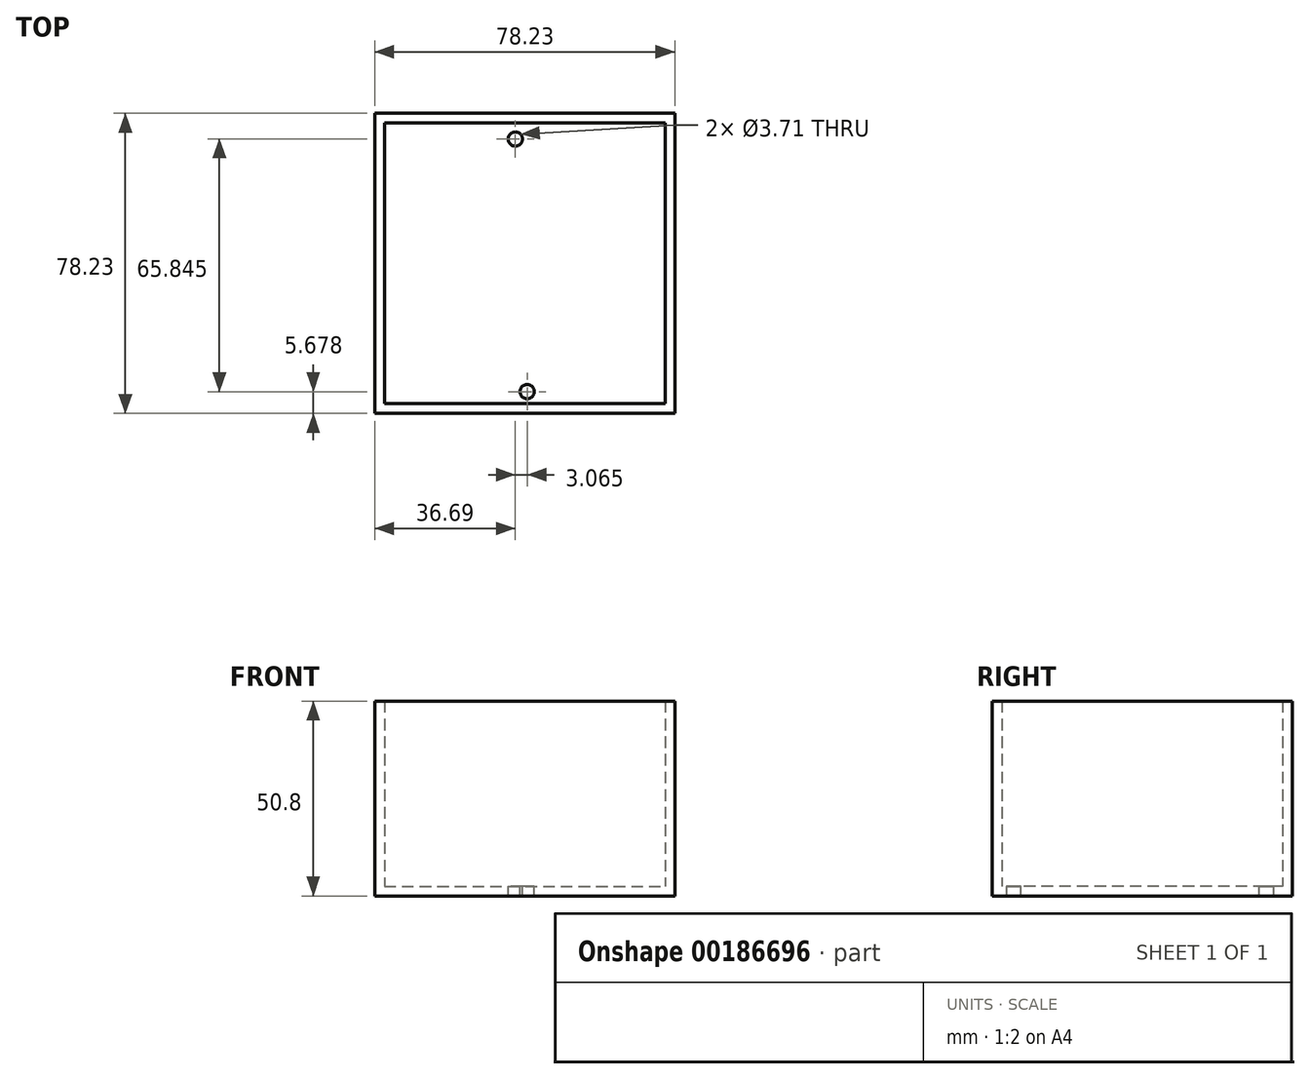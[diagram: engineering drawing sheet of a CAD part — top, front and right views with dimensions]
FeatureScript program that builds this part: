
annotation { "Feature Type Name" : "Feature", "Feature Type Description" : "" }
export const myFeature = defineFeature(function(context is Context, id is Id, definition is map)
    precondition{}
    {
        {
            var Q0;
            Q0=qCreatedBy(makeId("Top.planeOp"),FACE);
            var sketch = newSketch(context, id + "F0", { "sketchPlane" : qUnion([Q0])});
            skLineSegment(sketch, "E0.bottom", {"start": v(-42.74, 35.33) * mm, "end": v(35.49, 35.33) * mm});
            skLineSegment(sketch, "E0.top", {"start": v(-42.74, -42.9) * mm, "end": v(35.49, -42.9) * mm});
            skLineSegment(sketch, "E0.left", {"start": v(-42.74, 35.33) * mm, "end": v(-42.74, -42.9) * mm});
            skLineSegment(sketch, "E0.right", {"start": v(35.49, 35.33) * mm, "end": v(35.49, -42.9) * mm});
            skSolve(sketch);
        }
        {
            var Q0;
            Q0=makeQuery(id+"F0.imprint","IMPRINT",FACE,{"disambiguationData":[TD([[makeQuery(id+"F0.imprint","IMPRINT",EDGE,{"derivedFrom":sQuery(id+"F0.wireOp",EDGE,"E0.bottom")}),-1.0]])]});
            extrude(context, id + "F1", {"entities" : qUnion([Q0]), "depth" : 50.8 * mm});
        }
        {
            var Q0;
            Q0=makeQuery(id+"F1.opExtrude","CAP_FACE",FACE,{"disambiguationData":[OSD([sQuery(id+"F0.wireOp",EDGE,"E0.bottom"),sQuery(id+"F0.wireOp",EDGE,"E0.top"),sQuery(id+"F0.wireOp",EDGE,"E0.left"),sQuery(id+"F0.wireOp",EDGE,"E0.right")])],"isStart":false});
            shell(context, id + "F2", {"entities" : qUnion([Q0]), "thickness" : 2.54 * mm});
        }
        {
            var Q0;
            Q0=makeQuery(id+"F2.opShell","OFFSET_FACE",FACE,{"disambiguationData":[OSD([sQuery(id+"F0.wireOp",EDGE,"E0.bottom"),sQuery(id+"F0.wireOp",EDGE,"E0.top"),sQuery(id+"F0.wireOp",EDGE,"E0.left"),sQuery(id+"F0.wireOp",EDGE,"E0.right")])]});
            var sketch = newSketch(context, id + "F3", { "sketchPlane" : qUnion([Q0])});
            skCircle(sketch, "E1", {"center": v(-6.05, 28.62) * mm, "radius": 1.85 * mm});
            skSolve(sketch);
        }
        {
            var Q0;
            Q0=sQuery(id+"F3.wireOp",VERTEX,"E1.center");
            var Q1;
            Q1=makeQuery(id+"F1.opExtrude","SWEPT_BODY",BODY,{"disambiguationData":[OSD([sQuery(id+"F0.wireOp",EDGE,"E0.bottom"),sQuery(id+"F0.wireOp",EDGE,"E0.top"),sQuery(id+"F0.wireOp",EDGE,"E0.left"),sQuery(id+"F0.wireOp",EDGE,"E0.right")])]});
            hole(context, id + "F4", {"style" : HoleStyle.SIMPLE, "endStyle" : HoleEndStyle.THROUGH, "holeDiameter" : 3.7 * mm, "locations" : qUnion([Q0]), "scope" : qUnion([Q1]), "isTappedThrough" : true});
        }
        {
            var Q0;
            Q0=makeQuery(id+"F2.opShell","OFFSET_FACE",FACE,{"disambiguationData":[OSD([sQuery(id+"F0.wireOp",EDGE,"E0.bottom"),sQuery(id+"F0.wireOp",EDGE,"E0.top"),sQuery(id+"F0.wireOp",EDGE,"E0.left"),sQuery(id+"F0.wireOp",EDGE,"E0.right")])]});
            var sketch = newSketch(context, id + "F5", { "sketchPlane" : qUnion([Q0])});
            skCircle(sketch, "E2", {"center": v(-2.98, -37.22) * mm, "radius": 1.85 * mm});
            skSolve(sketch);
        }
        {
            var Q0;
            Q0=sQuery(id+"F5.wireOp",VERTEX,"E2.center");
            var Q1;
            Q1=makeQuery(id+"F1.opExtrude","SWEPT_BODY",BODY,{"disambiguationData":[OSD([sQuery(id+"F0.wireOp",EDGE,"E0.bottom"),sQuery(id+"F0.wireOp",EDGE,"E0.top"),sQuery(id+"F0.wireOp",EDGE,"E0.left"),sQuery(id+"F0.wireOp",EDGE,"E0.right")])]});
            hole(context, id + "F6", {"style" : HoleStyle.SIMPLE, "endStyle" : HoleEndStyle.THROUGH, "holeDiameter" : 3.7 * mm, "locations" : qUnion([Q0]), "scope" : qUnion([Q1]), "isTappedThrough" : true});
        }
    });
